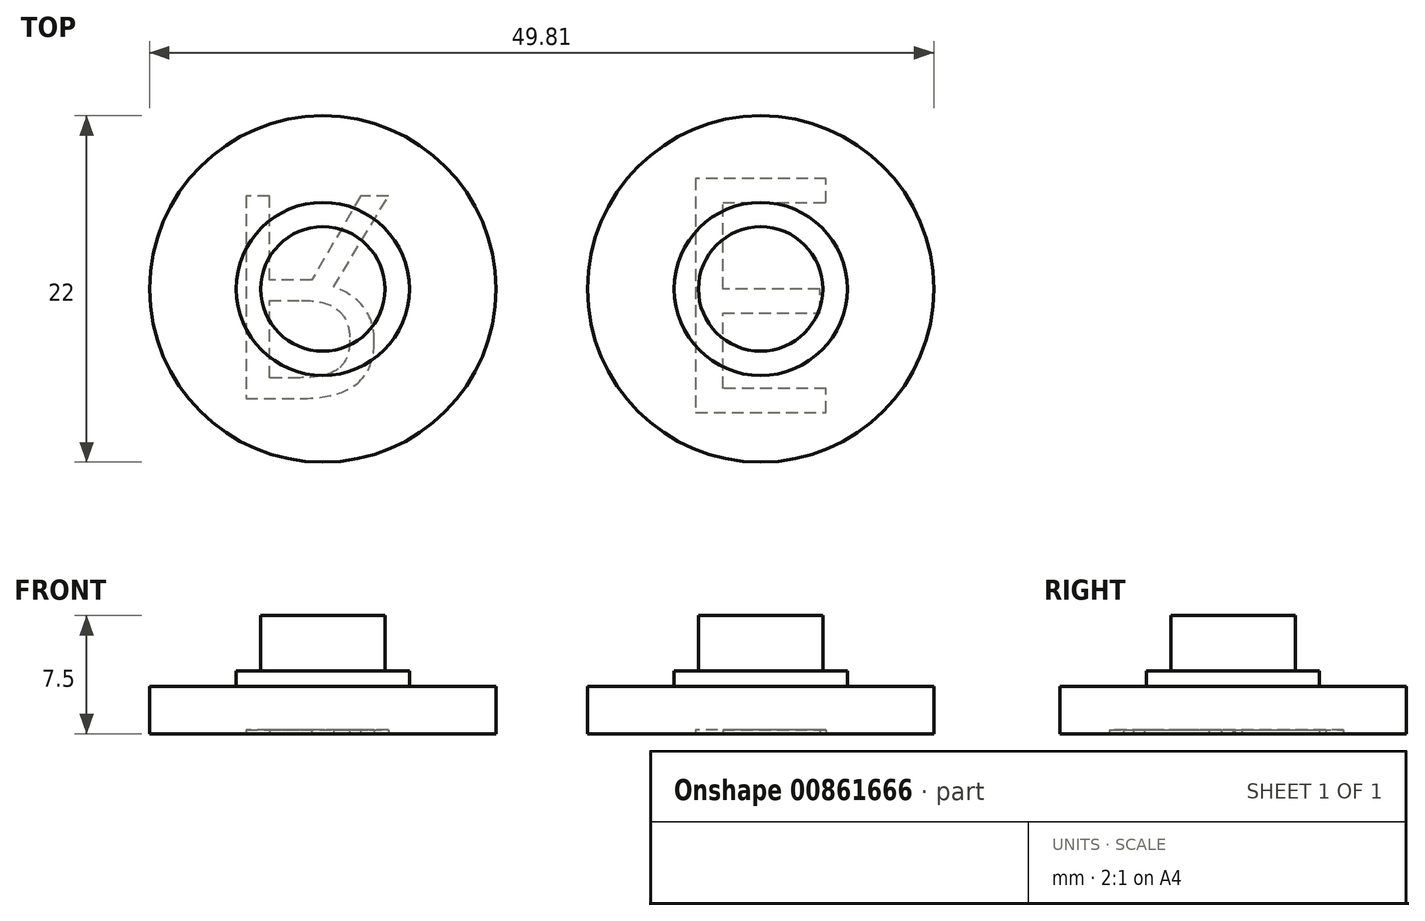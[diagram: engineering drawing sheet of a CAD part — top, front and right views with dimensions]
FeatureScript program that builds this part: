
annotation { "Feature Type Name" : "Feature", "Feature Type Description" : "" }
export const myFeature = defineFeature(function(context is Context, id is Id, definition is map)
    precondition{}
    {
        {
            var Q0;
            Q0=qCreatedBy(makeId("Front.planeOp"),FACE);
            var sketch = newSketch(context, id + "F0", { "sketchPlane" : qUnion([Q0])});
            skLineSegment(sketch, "E0", {"start": v(0, 7.5) * mm, "end": v(-3.95, 7.5) * mm});
            skLineSegment(sketch, "E1", {"start": v(-3.95, 7.5) * mm, "end": v(-3.95, 4) * mm});
            skLineSegment(sketch, "E2", {"start": v(-3.95, 4) * mm, "end": v(-5.5, 4) * mm});
            skLineSegment(sketch, "E3", {"start": v(-5.5, 4) * mm, "end": v(-5.5, 3) * mm});
            skLineSegment(sketch, "E4", {"start": v(-5.5, 3) * mm, "end": v(-11, 3) * mm});
            skLineSegment(sketch, "E5", {"start": v(-11, 3) * mm, "end": v(-11, 0) * mm});
            skLineSegment(sketch, "E6", {"start": v(-11, 0) * mm, "end": v(0, 0) * mm});
            skLineSegment(sketch, "E7", {"start": v(0, 0) * mm, "end": v(0, 7.5) * mm});
            skPoint(sketch, "E8.center.orphan", {"position": v(-420.56, -246.15) * mm});
            skPoint(sketch, "E8.end.orphan", {"position": v(-420.56, -275.96) * mm});
            skSolve(sketch);
        }
        {
            var Q0;
            Q0=qCreatedBy(makeId("Front.planeOp"),FACE);
            var sketch = newSketch(context, id + "F1", { "sketchPlane" : qUnion([Q0])});
            skLineSegment(sketch, "E9", {"start": v(-27.8, 0) * mm, "end": v(-27.8, 7.5) * mm});
            skLineSegment(sketch, "E10", {"start": v(-27.8, 7.5) * mm, "end": v(-31.76, 7.5) * mm});
            skLineSegment(sketch, "E11", {"start": v(-31.76, 7.5) * mm, "end": v(-31.76, 4) * mm});
            skLineSegment(sketch, "E12", {"start": v(-31.76, 4) * mm, "end": v(-33.3, 4) * mm});
            skLineSegment(sketch, "E13", {"start": v(-33.3, 4) * mm, "end": v(-33.3, 3) * mm});
            skLineSegment(sketch, "E14", {"start": v(-33.3, 3) * mm, "end": v(-38.8, 3) * mm});
            skLineSegment(sketch, "E15", {"start": v(-38.8, 3) * mm, "end": v(-38.8, 0) * mm});
            skLineSegment(sketch, "E16", {"start": v(-38.8, 0) * mm, "end": v(-27.8, 0) * mm});
            skSolve(sketch);
        }
        {
            var Q0;
            Q0=makeQuery(id+"F0.imprint","IMPRINT",FACE,{"disambiguationData":[TD([[makeQuery(id+"F0.imprint","IMPRINT",EDGE,{"derivedFrom":sQuery(id+"F0.wireOp",EDGE,"E0")}),1.0]])]});
            var Q1;
            Q1=sQuery(id+"F0.wireOp",EDGE,"E7");
            revolve(context, id + "F2", {"surfaceOperationType" : NewSurfaceOperationType.NEW, "entities" : qUnion([Q0]), "axis" : qUnion([Q1]), "revolveType" : RevolveType.FULL});
        }
        {
            var Q0;
            Q0=makeQuery(id+"F1.imprint","IMPRINT",FACE,{"disambiguationData":[TD([[makeQuery(id+"F1.imprint","IMPRINT",EDGE,{"derivedFrom":sQuery(id+"F1.wireOp",EDGE,"E9")}),1.0]])]});
            var Q1;
            Q1=sQuery(id+"F1.wireOp",EDGE,"E9");
            revolve(context, id + "F3", {"surfaceOperationType" : NewSurfaceOperationType.NEW, "entities" : qUnion([Q0]), "axis" : qUnion([Q1]), "revolveType" : RevolveType.FULL});
        }
        {
            var Q0;
            Q0=makeQuery(id+"F3.opRevolve","SWEPT_FACE",FACE,{"disambiguationData":[OSD([sQuery(id+"F1.wireOp",EDGE,"E16")])]});
            var sketch = newSketch(context, id + "F4", { "sketchPlane" : qUnion([Q0])});
            skText(sketch, "E17", { "text": "R", "fontName": "OpenSans-Regular.ttf"});
            const initialGuessF4  = {"E17": [-0.03446, -0.0059, 1, 0, 0.01296]};
            skSetInitialGuess(sketch, initialGuessF4);
            skSolve(sketch);
        }
        {
            var Q0;
            Q0=makeQuery(id+"F2.opRevolve","SWEPT_FACE",FACE,{"disambiguationData":[OSD([sQuery(id+"F0.wireOp",EDGE,"E6")])]});
            var sketch = newSketch(context, id + "F5", { "sketchPlane" : qUnion([Q0])});
            skText(sketch, "E18", { "text": "E\n", "fontName": "OpenSans-Regular.ttf"});
            const initialGuessF5  = {"E18": [-0.00617, -0.00702, 1, 0, 0.015]};
            skSetInitialGuess(sketch, initialGuessF5);
            skSolve(sketch);
        }
        {
            var Q0;
            Q0 = qSketchRegion(id + "F4", true);
            extrude(context, id + "F6", {"entities" : qUnion([Q0]), "operationType" : NewBodyOperationType.REMOVE, "oppositeDirection" : true, "depth" : 0.25 * mm, "offsetDistance" : 25 * mm});
        }
        {
            var Q0;
            Q0 = qSketchRegion(id + "F5", true);
            extrude(context, id + "F7", {"entities" : qUnion([Q0]), "operationType" : NewBodyOperationType.REMOVE, "oppositeDirection" : true, "depth" : 0.25 * mm, "offsetDistance" : 25 * mm});
        }
    });
